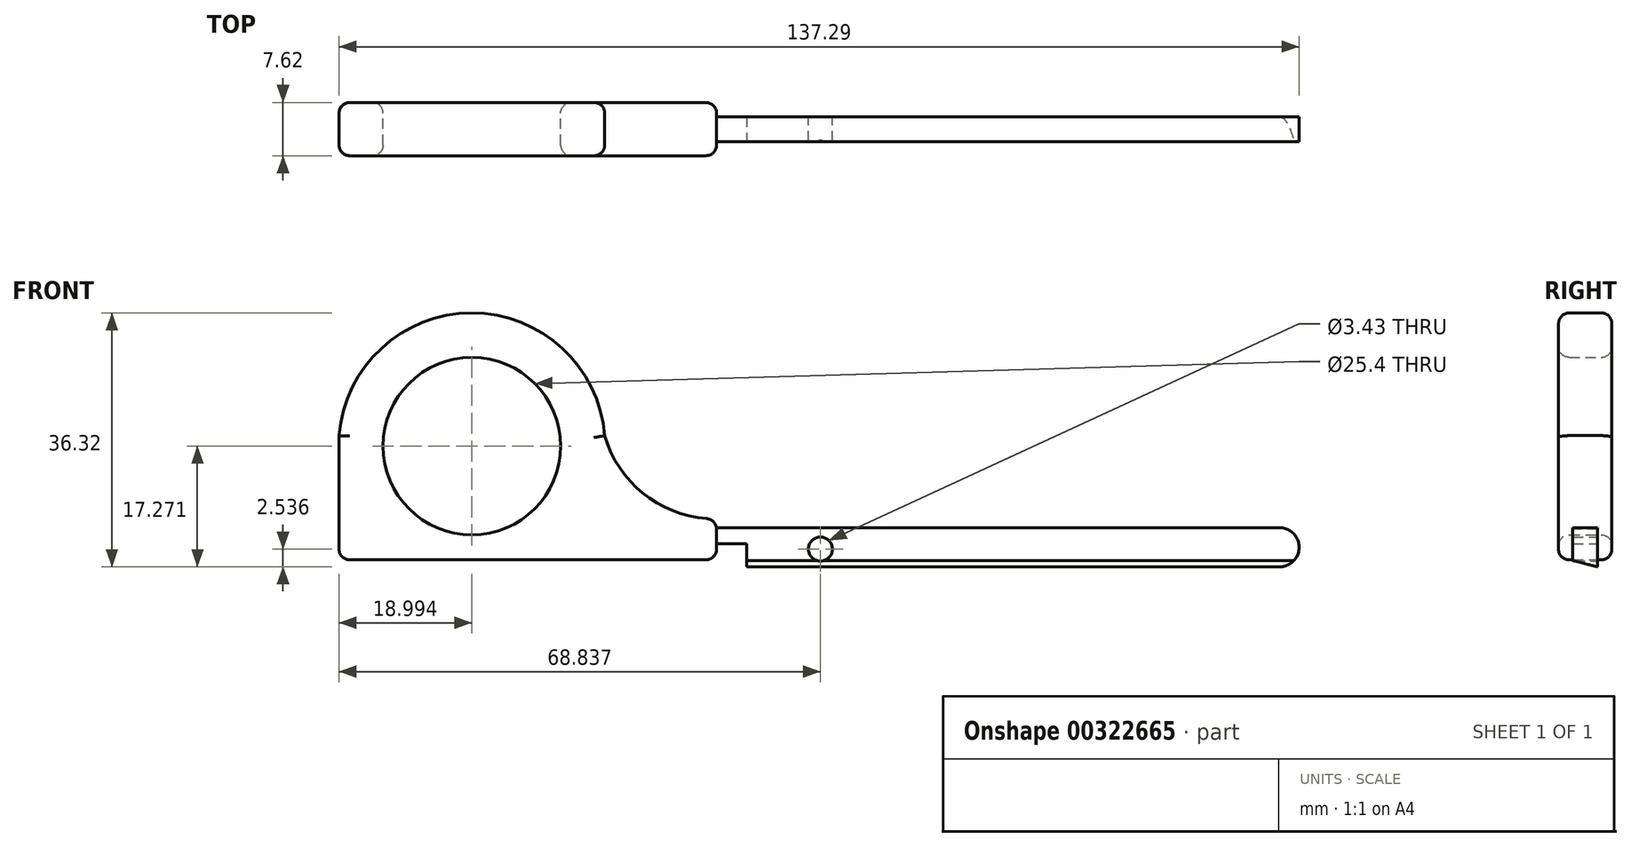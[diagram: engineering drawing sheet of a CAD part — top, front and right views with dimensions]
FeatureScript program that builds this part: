
annotation { "Feature Type Name" : "Feature", "Feature Type Description" : "" }
export const myFeature = defineFeature(function(context is Context, id is Id, definition is map)
    precondition{}
    {
        {
            var Q0;
            Q0=qCreatedBy(makeId("Front.planeOp"),FACE);
            var sketch = newSketch(context, id + "F0", { "sketchPlane" : qUnion([Q0])});
            skArc(sketch, "E0", {"start": v(-13.22, 18.69) * mm, "mid": v(-32.22, 36.24) * mm, "end": v(-51.2, 18.69) * mm});
            skLineSegment(sketch, "E1", {"start": v(-51.2, 18.69) * mm, "end": v(-51.2, 0.9) * mm});
            skLineSegment(sketch, "E2", {"start": v(-51.2, 0.9) * mm, "end": v(2.77, 0.9) * mm});
            skLineSegment(sketch, "E3", {"start": v(2.77, 0.9) * mm, "end": v(2.77, 6.77) * mm});
            skCircle(sketch, "E4", {"center": v(-32.22, 17.2) * mm, "radius": 12.7 * mm});
            skLineSegment(sketch, "E5", {"start": v(6.8, 7.3) * mm, "end": v(6.8, 7.3) * mm});
            skArc(sketch, "E6.filletArc", {"start": v(-13.22, 18.69) * mm, "mid": v(-5.52, 8.93) * mm, "end": v(6.8, 7.3) * mm});
            skSolve(sketch);
        }
        {
            var Q0;
            Q0 = qSketchRegion(id + "F0", true);
            extrude(context, id + "F1", {"entities" : qUnion([Q0]), "endBound" : BoundingType.SYMMETRIC, "depth" : 7.62 * mm});
        }
        {
            var Q0;
            Q0=makeQuery(id+"F1.opExtrude","CAP_EDGE",EDGE,{"disambiguationData":[OSD([sQuery(id+"F0.wireOp",EDGE,"9kog8hWk-n0xC-SFov-Do0S-5giGeTCsTdrN")])],"isStart":false});
            var Q1;
            Q1=makeQuery(id+"F1.opExtrude","CAP_EDGE",EDGE,{"disambiguationData":[OSD([sQuery(id+"F0.wireOp",EDGE,"9kog8hWk-n0xC-SFov-Do0S-5giGeTCsTdrN")])],"isStart":true});
            var Q2;
            Q2=makeQuery(id+"F1.opExtrude","CAP_EDGE",EDGE,{"disambiguationData":[OSD([sQuery(id+"F0.wireOp",EDGE,"E3")])],"isStart":false});
            var Q3;
            Q3=makeQuery(id+"F1.opExtrude","CAP_EDGE",EDGE,{"disambiguationData":[OSD([sQuery(id+"F0.wireOp",EDGE,"E2")])],"isStart":false});
            var Q4;
            Q4=makeQuery(id+"F1.opExtrude","SWEPT_EDGE",EDGE,{"disambiguationData":[OSD([sQuery(id+"F0.wireOp",EDGE,"E2"),sQuery(id+"F0.wireOp",EDGE,"E3")])]});
            var Q5;
            Q5=makeQuery(id+"F1.opExtrude","CAP_EDGE",EDGE,{"disambiguationData":[OSD([sQuery(id+"F0.wireOp",EDGE,"E4")])],"isStart":false});
            var Q6;
            Q6=makeQuery(id+"F1.opExtrude","CAP_EDGE",EDGE,{"disambiguationData":[OSD([sQuery(id+"F0.wireOp",EDGE,"E4")])],"isStart":true});
            var Q7;
            Q7=makeQuery(id+"F1.opExtrude","CAP_EDGE",EDGE,{"disambiguationData":[OSD([sQuery(id+"F0.wireOp",EDGE,"E1")])],"isStart":true});
            var Q8;
            Q8=makeQuery(id+"F1.opExtrude","CAP_EDGE",EDGE,{"disambiguationData":[OSD([sQuery(id+"F0.wireOp",EDGE,"E1")])],"isStart":false});
            var Q9;
            Q9=makeQuery(id+"F1.opExtrude","SWEPT_EDGE",EDGE,{"disambiguationData":[OSD([sQuery(id+"F0.wireOp",EDGE,"E1"),sQuery(id+"F0.wireOp",EDGE,"E2")])]});
            var Q10;
            Q10=makeQuery(id+"F1.opExtrude","CAP_EDGE",EDGE,{"disambiguationData":[OSD([sQuery(id+"F0.wireOp",EDGE,"E6.filletArc")])],"isStart":true});
            var Q11;
            Q11=makeQuery(id+"F1.opExtrude","CAP_EDGE",EDGE,{"disambiguationData":[OSD([sQuery(id+"F0.wireOp",EDGE,"E2")])],"isStart":true});
            var Q12;
            Q12=makeQuery(id+"F1.opExtrude","CAP_EDGE",EDGE,{"disambiguationData":[OSD([sQuery(id+"F0.wireOp",EDGE,"E3")])],"isStart":true});
            var Q13;
            Q13=makeQuery(id+"F1.opExtrude","CAP_EDGE",EDGE,{"disambiguationData":[OSD([sQuery(id+"F0.wireOp",EDGE,"E6.filletArc")])],"isStart":false});
            var Q14;
            Q14=makeQuery(id+"F1.opExtrude","CAP_EDGE",EDGE,{"disambiguationData":[OSD([sQuery(id+"F0.wireOp",EDGE,"E0")])],"isStart":false});
            var Q15;
            Q15=makeQuery(id+"F1.opExtrude","CAP_EDGE",EDGE,{"disambiguationData":[OSD([sQuery(id+"F0.wireOp",EDGE,"E0")])],"isStart":true});
            var Q16;
            Q16=makeQuery(id+"F1.opExtrude","SWEPT_EDGE",EDGE,{"disambiguationData":[OSD([sQuery(id+"F0.wireOp",EDGE,"E3"),sQuery(id+"F0.wireOp",EDGE,"E6.filletArc")])]});
            fillet(context, id + "F2", {"entities" : qUnion([Q0, Q1, Q2, Q3, Q4, Q5, Q6, Q7, Q8, Q9, Q10, Q11, Q12, Q13, Q14, Q15, Q16]), "radius" : 1.52 * mm, "tangentPropagation" : true, "allowEdgeOverflow" : false});
        }
        {
            var Q0;
            Q0=qCreatedBy(makeId("Front.planeOp"),FACE);
            var sketch = newSketch(context, id + "F3", { "sketchPlane" : qUnion([Q0])});
            skLineSegment(sketch, "E7", {"start": v(2.77, 5.5) * mm, "end": v(83.29, 5.5) * mm});
            skArc(sketch, "E8", {"start": v(83.29, -0.08) * mm, "mid": v(86.08, 2.71) * mm, "end": v(83.29, 5.5) * mm});
            skLineSegment(sketch, "E9", {"start": v(83.29, -0.08) * mm, "end": v(7.09, -0.08) * mm});
            skLineSegment(sketch, "E10", {"start": v(7.09, -0.08) * mm, "end": v(7.09, 3.22) * mm});
            skLineSegment(sketch, "E11", {"start": v(7.09, 3.22) * mm, "end": v(2.77, 3.22) * mm});
            skCircle(sketch, "E12", {"center": v(17.63, 2.46) * mm, "radius": 1.71 * mm});
            skLineSegment(sketch, "E13", {"start": v(2.77, 5.5) * mm, "end": v(2.77, 3.22) * mm});
            skSolve(sketch);
        }
        {
            var Q0;
            Q0 = qSketchRegion(id + "F3", true);
            extrude(context, id + "F4", {"entities" : qUnion([Q0]), "operationType" : NewBodyOperationType.ADD, "endBound" : BoundingType.SYMMETRIC, "depth" : 3.56 * mm});
        }
        {
            var Q0;
            Q0=makeQuery(id+"F4.opExtrude","CAP_FACE",FACE,{"disambiguationData":[OSD([sQuery(id+"F3.wireOp",EDGE,"E7"),sQuery(id+"F3.wireOp",EDGE,"E8"),sQuery(id+"F3.wireOp",EDGE,"E9"),sQuery(id+"F3.wireOp",EDGE,"E10"),sQuery(id+"F3.wireOp",EDGE,"E11"),sQuery(id+"F3.wireOp",EDGE,"E12"),sQuery(id+"F3.wireOp",EDGE,"E13")])],"isStart":false});
            var sketch = newSketch(context, id + "F5", { "sketchPlane" : qUnion([Q0])});
            skLineSegment(sketch, "E14", {"start": v(92.67, -2.67) * mm, "end": v(92.67, 7.28) * mm});
            skLineSegment(sketch, "E15", {"start": v(92.67, 7.28) * mm, "end": v(83.29, 7.28) * mm});
            skLineSegment(sketch, "E16", {"start": v(83.29, 7.28) * mm, "end": v(83.29, 5.5) * mm});
            skArc(sketch, "E17", {"start": v(86.08, 2.71) * mm, "mid": v(85.26, 4.69) * mm, "end": v(83.29, 5.5) * mm});
            skLineSegment(sketch, "E18", {"start": v(86.08, 2.71) * mm, "end": v(86.08, -2.5) * mm});
            skLineSegment(sketch, "E19", {"start": v(86.08, -2.5) * mm, "end": v(92.67, -2.67) * mm});
            skSolve(sketch);
        }
        {
            var Q0;
            Q0 = qSketchRegion(id + "F5", true);
            extrude(context, id + "F6", {"entities" : qUnion([Q0]), "operationType" : NewBodyOperationType.REMOVE, "endBound" : BoundingType.THROUGH_ALL, "oppositeDirection" : true, "depth" : 25.4 * mm});
        }
        {
            var Q0;
            Q0=makeQuery(id+"F4.opExtrude","SWEPT_FACE",FACE,{"disambiguationData":[OSD([sQuery(id+"F3.wireOp",EDGE,"E10")])]});
            var sketch = newSketch(context, id + "F7", { "sketchPlane" : qUnion([Q0])});
            skLineSegment(sketch, "E20", {"start": v(-1.78, -0.08) * mm, "end": v(1.78, 0.8) * mm});
            skLineSegment(sketch, "E21", {"start": v(1.78, 0.8) * mm, "end": v(1.78, -0.08) * mm});
            skLineSegment(sketch, "E22", {"start": v(1.78, -0.08) * mm, "end": v(-1.78, -0.08) * mm});
            skSolve(sketch);
        }
        {
            var Q0;
            Q0=makeQuery(id+"F7.imprint","IMPRINT",FACE,{"disambiguationData":[TD([[makeQuery(id+"F7.imprint","IMPRINT",EDGE,{"derivedFrom":sQuery(id+"F7.wireOp",EDGE,"E20")}),-1.0]])]});
            extrude(context, id + "F8", {"entities" : qUnion([Q0]), "operationType" : NewBodyOperationType.REMOVE, "endBound" : BoundingType.THROUGH_ALL, "oppositeDirection" : true, "depth" : 25.4 * mm});
        }
    });
